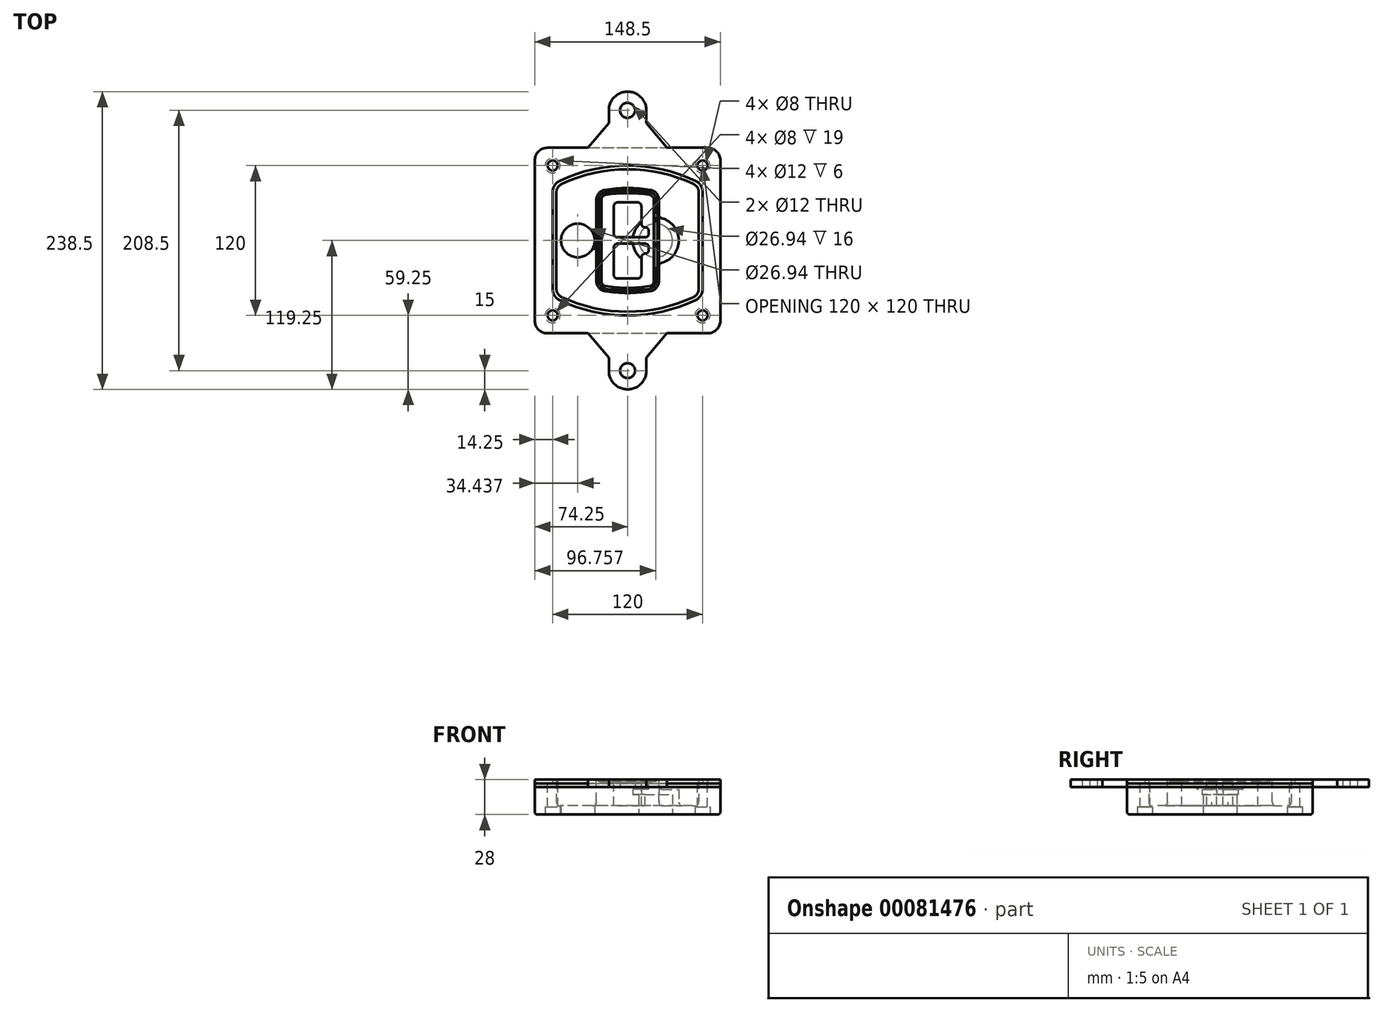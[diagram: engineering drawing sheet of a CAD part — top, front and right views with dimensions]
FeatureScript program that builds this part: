
annotation { "Feature Type Name" : "Feature", "Feature Type Description" : "" }
export const myFeature = defineFeature(function(context is Context, id is Id, definition is map)
    precondition{}
    {
        {
            var Q0;
            Q0=qCreatedBy(makeId("Top.planeOp"),FACE);
            var sketch = newSketch(context, id + "F0", { "sketchPlane" : qUnion([Q0])});
            skPoint(sketch, "E0.rect.middle", {"position": v(0, 0) * mm});
            skLineSegment(sketch, "E1.bottom", {"start": v(-64.25, -74.25) * mm, "end": v(64.25, -74.25) * mm});
            skLineSegment(sketch, "E1.top", {"start": v(-64.25, 74.25) * mm, "end": v(64.25, 74.25) * mm});
            skLineSegment(sketch, "E1.left", {"start": v(-74.25, -64.25) * mm, "end": v(-74.25, 64.25) * mm});
            skLineSegment(sketch, "E1.right", {"start": v(74.25, -64.25) * mm, "end": v(74.25, 64.25) * mm});
            skLineSegment(sketch, "E2", {"start": v(-74.25, 74.25) * mm, "end": v(74.25, -74.25) * mm, "construction": true});
            skLineSegment(sketch, "E3", {"start": v(74.25, 74.25) * mm, "end": v(-74.25, -74.25) * mm, "construction": true});
            skCircle(sketch, "E4", {"center": v(-60, 60) * mm, "radius": 4 * mm});
            skCircle(sketch, "E5", {"center": v(60, 60) * mm, "radius": 4 * mm});
            skCircle(sketch, "E6", {"center": v(60, -60) * mm, "radius": 4 * mm});
            skCircle(sketch, "E7", {"center": v(-60, -60) * mm, "radius": 4 * mm});
            skLineSegment(sketch, "E8", {"start": v(-60, 60) * mm, "end": v(60, 60) * mm, "construction": true});
            skLineSegment(sketch, "E9", {"start": v(60, 60) * mm, "end": v(60, -60) * mm, "construction": true});
            skLineSegment(sketch, "E10", {"start": v(60, -60) * mm, "end": v(-60, -60) * mm, "construction": true});
            skLineSegment(sketch, "E11", {"start": v(-60, -60) * mm, "end": v(-60, 60) * mm, "construction": true});
            skLineSegment(sketch, "E12", {"start": v(-60, 38.83) * mm, "end": v(-60, -38.83) * mm});
            skLineSegment(sketch, "E13", {"start": v(60, 38.83) * mm, "end": v(60, -38.83) * mm});
            skArc(sketch, "E14", {"start": v(54.26, 47.88) * mm, "mid": v(0, 60) * mm, "end": v(-54.26, 47.88) * mm});
            skArc(sketch, "E15", {"start": v(-54.26, -47.88) * mm, "mid": v(0, -60) * mm, "end": v(54.26, -47.88) * mm});
            skLineSegment(sketch, "E16", {"start": v(-60, 0) * mm, "end": v(60, 0) * mm, "construction": true});
            skPoint(sketch, "E17.visualSharp", {"position": v(-60, -45) * mm});
            skArc(sketch, "E17.filletArc", {"start": v(-60, -38.83) * mm, "mid": v(-58.44, -44.2) * mm, "end": v(-54.26, -47.88) * mm});
            skPoint(sketch, "E18.visualSharp", {"position": v(-60, 45) * mm});
            skArc(sketch, "E18.filletArc", {"start": v(-54.26, 47.88) * mm, "mid": v(-58.44, 44.2) * mm, "end": v(-60, 38.83) * mm});
            skPoint(sketch, "E19.visualSharp", {"position": v(60, 45) * mm});
            skArc(sketch, "E19.filletArc", {"start": v(60, 38.83) * mm, "mid": v(58.44, 44.2) * mm, "end": v(54.26, 47.88) * mm});
            skPoint(sketch, "E20.visualSharp", {"position": v(60, -45) * mm});
            skArc(sketch, "E20.filletArc", {"start": v(54.26, -47.88) * mm, "mid": v(58.44, -44.2) * mm, "end": v(60, -38.83) * mm});
            skPoint(sketch, "E21.visualSharp", {"position": v(-74.25, 74.25) * mm});
            skArc(sketch, "E21.filletArc", {"start": v(-64.25, 74.25) * mm, "mid": v(-71.32, 71.32) * mm, "end": v(-74.25, 64.25) * mm});
            skPoint(sketch, "E22.visualSharp", {"position": v(74.25, 74.25) * mm});
            skArc(sketch, "E22.filletArc", {"start": v(74.25, 64.25) * mm, "mid": v(71.32, 71.32) * mm, "end": v(64.25, 74.25) * mm});
            skPoint(sketch, "E23.visualSharp", {"position": v(74.25, -74.25) * mm});
            skArc(sketch, "E23.filletArc", {"start": v(64.25, -74.25) * mm, "mid": v(71.32, -71.32) * mm, "end": v(74.25, -64.25) * mm});
            skPoint(sketch, "E24.visualSharp", {"position": v(-74.25, -74.25) * mm});
            skArc(sketch, "E24.filletArc", {"start": v(-74.25, -64.25) * mm, "mid": v(-71.32, -71.32) * mm, "end": v(-64.25, -74.25) * mm});
            skArc(sketch, "E25.0", {"start": v(57, 38.83) * mm, "mid": v(55.9, 42.58) * mm, "end": v(52.98, 45.17) * mm});
            skLineSegment(sketch, "E25.1", {"start": v(57, 38.83) * mm, "end": v(57, -38.83) * mm});
            skArc(sketch, "E25.2", {"start": v(52.98, -45.17) * mm, "mid": v(55.9, -42.58) * mm, "end": v(57, -38.83) * mm});
            skArc(sketch, "E25.3", {"start": v(-52.98, -45.17) * mm, "mid": v(0, -57) * mm, "end": v(52.98, -45.17) * mm});
            skArc(sketch, "E25.4", {"start": v(-57, -38.83) * mm, "mid": v(-55.9, -42.58) * mm, "end": v(-52.98, -45.17) * mm});
            skArc(sketch, "E25.5", {"start": v(52.98, 45.17) * mm, "mid": v(0, 57) * mm, "end": v(-52.98, 45.17) * mm});
            skLineSegment(sketch, "E25.6", {"start": v(-57, 38.83) * mm, "end": v(-57, -38.83) * mm});
            skArc(sketch, "E25.7", {"start": v(-52.98, 45.17) * mm, "mid": v(-55.9, 42.58) * mm, "end": v(-57, 38.83) * mm});
            skArc(sketch, "E26.0", {"start": v(-55.96, 51.5) * mm, "mid": v(-61.82, 46.33) * mm, "end": v(-64, 38.83) * mm});
            skArc(sketch, "E26.1", {"start": v(55.96, 51.5) * mm, "mid": v(0, 64) * mm, "end": v(-55.96, 51.5) * mm});
            skArc(sketch, "E26.2", {"start": v(64, 38.83) * mm, "mid": v(61.82, 46.33) * mm, "end": v(55.96, 51.5) * mm});
            skLineSegment(sketch, "E26.3", {"start": v(64, 38.83) * mm, "end": v(64, -38.83) * mm});
            skArc(sketch, "E26.4", {"start": v(55.96, -51.5) * mm, "mid": v(61.82, -46.33) * mm, "end": v(64, -38.83) * mm});
            skLineSegment(sketch, "E26.5", {"start": v(-64, 38.83) * mm, "end": v(-64, -38.83) * mm});
            skArc(sketch, "E26.6", {"start": v(-55.96, -51.5) * mm, "mid": v(0, -64) * mm, "end": v(55.96, -51.5) * mm});
            skArc(sketch, "E26.7", {"start": v(-64, -38.83) * mm, "mid": v(-61.82, -46.33) * mm, "end": v(-55.96, -51.5) * mm});
            skSolve(sketch);
        }
        {
            var Q0;
            Q0=makeQuery(id+"F0.imprint","IMPRINT",FACE,{"disambiguationData":[TD([[makeQuery(id+"F0.imprint","IMPRINT",EDGE,{"derivedFrom":sQuery(id+"F0.wireOp",EDGE,"E1.bottom")}),1.0]])]});
            var Q1;
            Q1=makeQuery(id+"F0.imprint","IMPRINT",FACE,{"disambiguationData":[TD([[makeQuery(id+"F0.imprint","IMPRINT",EDGE,{"derivedFrom":sQuery(id+"F0.wireOp",EDGE,"E12")}),1.0]])]});
            var Q2;
            Q2=makeQuery(id+"F0.imprint","IMPRINT",FACE,{"disambiguationData":[TD([[makeQuery(id+"F0.imprint","IMPRINT",EDGE,{"derivedFrom":sQuery(id+"F0.wireOp",EDGE,"E25.0")}),1.0]])]});
            var Q3;
            Q3=makeQuery(id+"F0.imprint","IMPRINT",FACE,{"disambiguationData":[TD([[makeQuery(id+"F0.imprint","IMPRINT",EDGE,{"derivedFrom":sQuery(id+"F0.wireOp",EDGE,"E12")}),-1.0]])]});
            extrude(context, id + "F1", {"entities" : qUnion([Q0, Q1, Q2, Q3]), "oppositeDirection" : true, "depth" : 25 * mm});
        }
        {
            var Q0;
            Q0=makeQuery(id+"F0.imprint","IMPRINT",FACE,{"disambiguationData":[TD([[makeQuery(id+"F0.imprint","IMPRINT",EDGE,{"derivedFrom":sQuery(id+"F0.wireOp",EDGE,"E12")}),1.0]])]});
            extrude(context, id + "F2", {"entities" : qUnion([Q0]), "operationType" : NewBodyOperationType.ADD, "depth" : 3 * mm});
        }
        {
            var Q0;
            Q0=makeQuery(id+"F0.imprint","IMPRINT",FACE,{"disambiguationData":[TD([[makeQuery(id+"F0.imprint","IMPRINT",EDGE,{"derivedFrom":sQuery(id+"F0.wireOp",EDGE,"E25.0")}),1.0]])]});
            extrude(context, id + "F3", {"entities" : qUnion([Q0]), "operationType" : NewBodyOperationType.REMOVE, "oppositeDirection" : true, "depth" : 18 * mm});
        }
        {
            var Q0;
            Q0=makeQuery(id+"F2.opExtrude","CAP_FACE",FACE,{"disambiguationData":[OSD([sQuery(id+"F0.wireOp",EDGE,"E12"),sQuery(id+"F0.wireOp",EDGE,"E13"),sQuery(id+"F0.wireOp",EDGE,"E14"),sQuery(id+"F0.wireOp",EDGE,"E15"),sQuery(id+"F0.wireOp",EDGE,"E17.filletArc"),sQuery(id+"F0.wireOp",EDGE,"E18.filletArc"),sQuery(id+"F0.wireOp",EDGE,"E19.filletArc"),sQuery(id+"F0.wireOp",EDGE,"E20.filletArc"),sQuery(id+"F0.wireOp",EDGE,"E25.0"),sQuery(id+"F0.wireOp",EDGE,"E25.1"),sQuery(id+"F0.wireOp",EDGE,"E25.2"),sQuery(id+"F0.wireOp",EDGE,"E25.3"),sQuery(id+"F0.wireOp",EDGE,"E25.4"),sQuery(id+"F0.wireOp",EDGE,"E25.5"),sQuery(id+"F0.wireOp",EDGE,"E25.6"),sQuery(id+"F0.wireOp",EDGE,"E25.7")])],"isStart":false});
            var sketch = newSketch(context, id + "F4", { "sketchPlane" : qUnion([Q0])});
            skArc(sketch, "E27.0", {"start": v(-18.34, -40.45) * mm, "mid": v(0, -42) * mm, "end": v(18.34, -40.45) * mm});
            skArc(sketch, "E28.0", {"start": v(18.34, 40.45) * mm, "mid": v(0, 42) * mm, "end": v(-18.34, 40.45) * mm});
            skLineSegment(sketch, "E29", {"start": v(-25, 32.57) * mm, "end": v(-25, -32.57) * mm});
            skLineSegment(sketch, "E30", {"start": v(25, 32.57) * mm, "end": v(25, -32.57) * mm});
            skLineSegment(sketch, "E31", {"start": v(-25, 39.1) * mm, "end": v(25, 39.1) * mm, "construction": true});
            skLineSegment(sketch, "E32", {"start": v(-25, -39.1) * mm, "end": v(25, -39.1) * mm, "construction": true});
            skPoint(sketch, "E33.visualSharp", {"position": v(-25, 39.1) * mm});
            skArc(sketch, "E33.filletArc", {"start": v(-18.34, 40.45) * mm, "mid": v(-23.11, 37.73) * mm, "end": v(-25, 32.57) * mm});
            skPoint(sketch, "E34.visualSharp", {"position": v(25, 39.1) * mm});
            skArc(sketch, "E34.filletArc", {"start": v(25, 32.57) * mm, "mid": v(23.11, 37.73) * mm, "end": v(18.34, 40.45) * mm});
            skPoint(sketch, "E35.visualSharp", {"position": v(25, -39.1) * mm});
            skArc(sketch, "E35.filletArc", {"start": v(18.34, -40.45) * mm, "mid": v(23.11, -37.73) * mm, "end": v(25, -32.57) * mm});
            skPoint(sketch, "E36.visualSharp", {"position": v(-25, -39.1) * mm});
            skArc(sketch, "E36.filletArc", {"start": v(-25, -32.57) * mm, "mid": v(-23.11, -37.73) * mm, "end": v(-18.34, -40.45) * mm});
            skArc(sketch, "E37.0", {"start": v(52.98, 45.17) * mm, "mid": v(0, 57) * mm, "end": v(-52.98, 45.17) * mm});
            skArc(sketch, "E37.1", {"start": v(-52.98, 45.17) * mm, "mid": v(-55.9, 42.58) * mm, "end": v(-57, 38.83) * mm});
            skLineSegment(sketch, "E37.2", {"start": v(-57, 38.83) * mm, "end": v(-57, -38.83) * mm});
            skArc(sketch, "E37.3", {"start": v(-57, -38.83) * mm, "mid": v(-55.9, -42.58) * mm, "end": v(-52.98, -45.17) * mm});
            skArc(sketch, "E37.4", {"start": v(-52.98, -45.17) * mm, "mid": v(0, -57) * mm, "end": v(52.98, -45.17) * mm});
            skArc(sketch, "E37.5", {"start": v(52.98, -45.17) * mm, "mid": v(55.9, -42.58) * mm, "end": v(57, -38.83) * mm});
            skLineSegment(sketch, "E37.6", {"start": v(57, 38.83) * mm, "end": v(57, -38.83) * mm});
            skArc(sketch, "E37.7", {"start": v(57, 38.83) * mm, "mid": v(55.9, 42.58) * mm, "end": v(52.98, 45.17) * mm});
            skLineSegment(sketch, "E38.0", {"start": v(23, 32.57) * mm, "end": v(23, -32.57) * mm});
            skArc(sketch, "E38.1", {"start": v(18, -38.48) * mm, "mid": v(21.58, -36.44) * mm, "end": v(23, -32.57) * mm});
            skArc(sketch, "E38.2", {"start": v(-18, -38.48) * mm, "mid": v(0, -40) * mm, "end": v(18, -38.48) * mm});
            skArc(sketch, "E38.3", {"start": v(-23, -32.57) * mm, "mid": v(-21.58, -36.44) * mm, "end": v(-18, -38.48) * mm});
            skLineSegment(sketch, "E38.4", {"start": v(-23, 32.57) * mm, "end": v(-23, -32.57) * mm});
            skArc(sketch, "E38.5", {"start": v(23, 32.57) * mm, "mid": v(21.58, 36.44) * mm, "end": v(18, 38.48) * mm});
            skArc(sketch, "E38.6", {"start": v(-18, 38.48) * mm, "mid": v(-21.58, 36.44) * mm, "end": v(-23, 32.57) * mm});
            skArc(sketch, "E38.7", {"start": v(18, 38.48) * mm, "mid": v(0, 40) * mm, "end": v(-18, 38.48) * mm});
            skArc(sketch, "E39.0", {"start": v(21, 32.57) * mm, "mid": v(20.06, 35.15) * mm, "end": v(17.67, 36.5) * mm});
            skLineSegment(sketch, "E39.1", {"start": v(21, 32.57) * mm, "end": v(21, -32.57) * mm});
            skArc(sketch, "E39.2", {"start": v(17.67, -36.5) * mm, "mid": v(20.06, -35.15) * mm, "end": v(21, -32.57) * mm});
            skArc(sketch, "E39.3", {"start": v(-17.67, -36.5) * mm, "mid": v(0, -38) * mm, "end": v(17.67, -36.5) * mm});
            skArc(sketch, "E39.4", {"start": v(-21, -32.57) * mm, "mid": v(-20.06, -35.15) * mm, "end": v(-17.67, -36.5) * mm});
            skArc(sketch, "E39.5", {"start": v(17.67, 36.5) * mm, "mid": v(0, 38) * mm, "end": v(-17.67, 36.5) * mm});
            skLineSegment(sketch, "E39.6", {"start": v(-21, 32.57) * mm, "end": v(-21, -32.57) * mm});
            skArc(sketch, "E39.7", {"start": v(-17.67, 36.5) * mm, "mid": v(-20.06, 35.15) * mm, "end": v(-21, 32.57) * mm});
            skLineSegment(sketch, "E40", {"start": v(-25, 0) * mm, "end": v(25, 0) * mm, "construction": true});
            skLineSegment(sketch, "E41", {"start": v(-11, 5.5) * mm, "end": v(-11, 27.5) * mm});
            skLineSegment(sketch, "E42", {"start": v(-8, 30.5) * mm, "end": v(8, 30.5) * mm});
            skLineSegment(sketch, "E43", {"start": v(11, 27.5) * mm, "end": v(11, 13.5) * mm});
            skLineSegment(sketch, "E44", {"start": v(14, 10.5) * mm, "end": v(14, 10.5) * mm});
            skLineSegment(sketch, "E45", {"start": v(17, 7.5) * mm, "end": v(17, 5.5) * mm});
            skLineSegment(sketch, "E46", {"start": v(14, 2.5) * mm, "end": v(-8, 2.5) * mm});
            skPoint(sketch, "E47.visualSharp", {"position": v(-11, 30.5) * mm});
            skArc(sketch, "E47.filletArc", {"start": v(-8, 30.5) * mm, "mid": v(-10.12, 29.62) * mm, "end": v(-11, 27.5) * mm});
            skPoint(sketch, "E48.visualSharp", {"position": v(11, 30.5) * mm});
            skArc(sketch, "E48.filletArc", {"start": v(11, 27.5) * mm, "mid": v(10.12, 29.62) * mm, "end": v(8, 30.5) * mm});
            skPoint(sketch, "E49.visualSharp", {"position": v(11, 10.5) * mm});
            skArc(sketch, "E49.filletArc", {"start": v(11, 13.5) * mm, "mid": v(11.88, 11.38) * mm, "end": v(14, 10.5) * mm});
            skPoint(sketch, "E50.visualSharp", {"position": v(17, 10.5) * mm});
            skArc(sketch, "E50.filletArc", {"start": v(17, 7.5) * mm, "mid": v(16.12, 9.62) * mm, "end": v(14, 10.5) * mm});
            skPoint(sketch, "E51.visualSharp", {"position": v(17, 2.5) * mm});
            skArc(sketch, "E51.filletArc", {"start": v(14, 2.5) * mm, "mid": v(16.12, 3.38) * mm, "end": v(17, 5.5) * mm});
            skPoint(sketch, "E52.visualSharp", {"position": v(-11, 2.5) * mm});
            skArc(sketch, "E52.filletArc", {"start": v(-11, 5.5) * mm, "mid": v(-10.12, 3.38) * mm, "end": v(-8, 2.5) * mm});
            skLineSegment(sketch, "E53.0.MirrorCS", {"start": v(14, -2.5) * mm, "end": v(-8, -2.5) * mm});
            skArc(sketch, "E54.0.MirrorCS", {"start": v(-11, -5.5) * mm, "mid": v(-10.12, -3.38) * mm, "end": v(-8, -2.5) * mm});
            skLineSegment(sketch, "E55.0.MirrorCS", {"start": v(-11, -5.5) * mm, "end": v(-11, -27.5) * mm});
            skArc(sketch, "E56.0.MirrorCS", {"start": v(-8, -30.5) * mm, "mid": v(-10.12, -29.62) * mm, "end": v(-11, -27.5) * mm});
            skLineSegment(sketch, "E57.0.MirrorCS", {"start": v(-8, -30.5) * mm, "end": v(8, -30.5) * mm});
            skArc(sketch, "E58.0.MirrorCS", {"start": v(11, -27.5) * mm, "mid": v(10.12, -29.62) * mm, "end": v(8, -30.5) * mm});
            skLineSegment(sketch, "E59.0.MirrorCS", {"start": v(11, -27.5) * mm, "end": v(11, -13.5) * mm});
            skArc(sketch, "E60.0.MirrorCS", {"start": v(11, -13.5) * mm, "mid": v(11.88, -11.38) * mm, "end": v(14, -10.5) * mm});
            skArc(sketch, "E61.0.MirrorCS", {"start": v(17, -7.5) * mm, "mid": v(16.12, -9.62) * mm, "end": v(14, -10.5) * mm});
            skLineSegment(sketch, "E62.0.MirrorCS", {"start": v(17, -7.5) * mm, "end": v(17, -5.5) * mm});
            skArc(sketch, "E63.0.MirrorCS", {"start": v(14, -2.5) * mm, "mid": v(16.12, -3.38) * mm, "end": v(17, -5.5) * mm});
            skSolve(sketch);
        }
        {
            var Q0;
            Q0=makeQuery(id+"F4.imprint","IMPRINT",FACE,{"disambiguationData":[TD([[makeQuery(id+"F4.imprint","IMPRINT",EDGE,{"derivedFrom":sQuery(id+"F4.wireOp",EDGE,"E27.0")}),1.0]])]});
            var Q1;
            Q1=makeQuery(id+"F4.imprint","IMPRINT",FACE,{"disambiguationData":[TD([[makeQuery(id+"F4.imprint","IMPRINT",EDGE,{"derivedFrom":sQuery(id+"F4.wireOp",EDGE,"E38.0")}),-1.0]])]});
            var Q2;
            Q2=makeQuery(id+"F4.imprint","IMPRINT",FACE,{"disambiguationData":[TD([[makeQuery(id+"F4.imprint","IMPRINT",EDGE,{"derivedFrom":sQuery(id+"F4.wireOp",EDGE,"E39.0")}),1.0]])]});
            extrude(context, id + "F5", {"entities" : qUnion([Q0, Q1, Q2]), "operationType" : NewBodyOperationType.ADD, "endBound" : BoundingType.UP_TO_NEXT, "oppositeDirection" : true, "depth" : 25 * mm});
        }
        {
            var Q0;
            Q0=makeQuery(id+"F4.imprint","IMPRINT",FACE,{"disambiguationData":[TD([[makeQuery(id+"F4.imprint","IMPRINT",EDGE,{"derivedFrom":sQuery(id+"F4.wireOp",EDGE,"E38.0")}),-1.0]])]});
            extrude(context, id + "F6", {"entities" : qUnion([Q0]), "operationType" : NewBodyOperationType.REMOVE, "oppositeDirection" : true, "depth" : 2 * mm});
        }
        {
            var Q0;
            Q0=makeQuery(id+"F1.opExtrude","CAP_FACE",FACE,{"disambiguationData":[OSD([sQuery(id+"F0.wireOp",EDGE,"E1.bottom"),sQuery(id+"F0.wireOp",EDGE,"E1.top"),sQuery(id+"F0.wireOp",EDGE,"E1.left"),sQuery(id+"F0.wireOp",EDGE,"E1.right"),sQuery(id+"F0.wireOp",EDGE,"E4"),sQuery(id+"F0.wireOp",EDGE,"E5"),sQuery(id+"F0.wireOp",EDGE,"E6"),sQuery(id+"F0.wireOp",EDGE,"E7"),sQuery(id+"F0.wireOp",EDGE,"E21.filletArc"),sQuery(id+"F0.wireOp",EDGE,"E22.filletArc"),sQuery(id+"F0.wireOp",EDGE,"E23.filletArc"),sQuery(id+"F0.wireOp",EDGE,"E24.filletArc")])],"isStart":false});
            var sketch = newSketch(context, id + "F7", { "sketchPlane" : qUnion([Q0])});
            skCircle(sketch, "E64", {"center": v(22.5, 0) * mm, "radius": 13.47 * mm});
            skCircle(sketch, "E65", {"center": v(-39.81, 0) * mm, "radius": 13.47 * mm});
            skLineSegment(sketch, "E66", {"start": v(74.25, 0) * mm, "end": v(-74.25, 0) * mm});
            skCircle(sketch, "E67", {"center": v(22.5, 0) * mm, "radius": 18.47 * mm});
            skCircle(sketch, "E68", {"center": v(60, -60) * mm, "radius": 6 * mm});
            skCircle(sketch, "E69", {"center": v(-60, -60) * mm, "radius": 6 * mm});
            skCircle(sketch, "E70", {"center": v(-60, 60) * mm, "radius": 6 * mm});
            skCircle(sketch, "E71", {"center": v(60, 60) * mm, "radius": 6 * mm});
            skSolve(sketch);
        }
        {
            var Q0;
            {var subQ1=sQuery(id+"F7.wireOp",EDGE,"E66");var subQ4=sQuery(id+"F7.wireOp",EDGE,"E64");var subQ6=makeQuery(id+"F7.imprint","INTERSECT",VERTEX,{"disambiguationData":[OD(0.0)],"derivedFrom":[subQ4,subQ1]});Q0=makeQuery(id+"F7.imprint","IMPRINT",FACE,{"disambiguationData":[TD([[makeQuery(id+"F7.imprint","IMPRINT",EDGE,{"disambiguationData":[TD([[subQ6,-1.0]])],"derivedFrom":subQ4}),-1.0]])]});}
            var Q1;
            {var subQ0=sQuery(id+"F7.wireOp",EDGE,"E66");var subQ1=sQuery(id+"F7.wireOp",EDGE,"E64");var subQ3=makeQuery(id+"F7.imprint","INTERSECT",VERTEX,{"disambiguationData":[OD(0.0)],"derivedFrom":[subQ1,subQ0]});Q1=makeQuery(id+"F7.imprint","IMPRINT",FACE,{"disambiguationData":[TD([[makeQuery(id+"F7.imprint","IMPRINT",EDGE,{"disambiguationData":[TD([[subQ3,-1.0]])],"derivedFrom":subQ1}),1.0]])]});}
            var Q2;
            {var subQ0=sQuery(id+"F7.wireOp",EDGE,"E66");var subQ1=sQuery(id+"F7.wireOp",EDGE,"E64");var subQ3=makeQuery(id+"F7.imprint","INTERSECT",VERTEX,{"disambiguationData":[OD(0.0)],"derivedFrom":[subQ1,subQ0]});Q2=makeQuery(id+"F7.imprint","IMPRINT",FACE,{"disambiguationData":[TD([[makeQuery(id+"F7.imprint","IMPRINT",EDGE,{"disambiguationData":[TD([[subQ3,1.0]])],"derivedFrom":subQ1}),1.0]])]});}
            var Q3;
            {var subQ1=sQuery(id+"F7.wireOp",EDGE,"E66");var subQ4=sQuery(id+"F7.wireOp",EDGE,"E64");var subQ6=makeQuery(id+"F7.imprint","INTERSECT",VERTEX,{"disambiguationData":[OD(0.0)],"derivedFrom":[subQ4,subQ1]});Q3=makeQuery(id+"F7.imprint","IMPRINT",FACE,{"disambiguationData":[TD([[makeQuery(id+"F7.imprint","IMPRINT",EDGE,{"disambiguationData":[TD([[subQ6,1.0]])],"derivedFrom":subQ4}),-1.0]])]});}
            extrude(context, id + "F8", {"entities" : qUnion([Q0, Q1, Q2, Q3]), "operationType" : NewBodyOperationType.ADD, "oppositeDirection" : true, "depth" : 20 * mm});
        }
        {
            var Q0;
            {var subQ0=sQuery(id+"F7.wireOp",EDGE,"E66");var subQ1=sQuery(id+"F7.wireOp",EDGE,"E64");var subQ3=makeQuery(id+"F7.imprint","INTERSECT",VERTEX,{"disambiguationData":[OD(0.0)],"derivedFrom":[subQ1,subQ0]});Q0=makeQuery(id+"F7.imprint","IMPRINT",FACE,{"disambiguationData":[TD([[makeQuery(id+"F7.imprint","IMPRINT",EDGE,{"disambiguationData":[TD([[subQ3,-1.0]])],"derivedFrom":subQ1}),1.0]])]});}
            var Q1;
            {var subQ0=sQuery(id+"F7.wireOp",EDGE,"E66");var subQ1=sQuery(id+"F7.wireOp",EDGE,"E64");var subQ3=makeQuery(id+"F7.imprint","INTERSECT",VERTEX,{"disambiguationData":[OD(0.0)],"derivedFrom":[subQ1,subQ0]});Q1=makeQuery(id+"F7.imprint","IMPRINT",FACE,{"disambiguationData":[TD([[makeQuery(id+"F7.imprint","IMPRINT",EDGE,{"disambiguationData":[TD([[subQ3,1.0]])],"derivedFrom":subQ1}),1.0]])]});}
            extrude(context, id + "F9", {"entities" : qUnion([Q0, Q1]), "operationType" : NewBodyOperationType.REMOVE, "oppositeDirection" : true, "depth" : 16 * mm});
        }
        {
            var Q0;
            {var subQ0=sQuery(id+"F7.wireOp",EDGE,"E66");var subQ1=sQuery(id+"F7.wireOp",EDGE,"E65");var subQ3=makeQuery(id+"F7.imprint","INTERSECT",VERTEX,{"disambiguationData":[OD(0.0)],"derivedFrom":[subQ1,subQ0]});Q0=makeQuery(id+"F7.imprint","IMPRINT",FACE,{"disambiguationData":[TD([[makeQuery(id+"F7.imprint","IMPRINT",EDGE,{"disambiguationData":[TD([[subQ3,-1.0]])],"derivedFrom":subQ1}),1.0]])]});}
            var Q1;
            {var subQ0=sQuery(id+"F7.wireOp",EDGE,"E66");var subQ1=sQuery(id+"F7.wireOp",EDGE,"E65");var subQ3=makeQuery(id+"F7.imprint","INTERSECT",VERTEX,{"disambiguationData":[OD(0.0)],"derivedFrom":[subQ1,subQ0]});Q1=makeQuery(id+"F7.imprint","IMPRINT",FACE,{"disambiguationData":[TD([[makeQuery(id+"F7.imprint","IMPRINT",EDGE,{"disambiguationData":[TD([[subQ3,1.0]])],"derivedFrom":subQ1}),1.0]])]});}
            extrude(context, id + "F10", {"entities" : qUnion([Q0, Q1]), "operationType" : NewBodyOperationType.REMOVE, "oppositeDirection" : true, "depth" : 25 * mm});
        }
        {
            var Q0;
            Q0=makeQuery(id+"F7.imprint","IMPRINT",FACE,{"disambiguationData":[TD([[makeQuery(id+"F7.imprint","IMPRINT",EDGE,{"derivedFrom":sQuery(id+"F7.wireOp",EDGE,"E68")}),1.0]])]});
            var Q1;
            Q1=makeQuery(id+"F7.imprint","IMPRINT",FACE,{"disambiguationData":[TD([[makeQuery(id+"F7.imprint","IMPRINT",EDGE,{"derivedFrom":makeQuery(id+"F1.opExtrude","CAP_EDGE",EDGE,{"disambiguationData":[OSD([sQuery(id+"F0.wireOp",EDGE,"E5")])],"isStart":false})}),-1.0]])]});
            var Q2;
            Q2=makeQuery(id+"F7.imprint","IMPRINT",FACE,{"disambiguationData":[TD([[makeQuery(id+"F7.imprint","IMPRINT",EDGE,{"derivedFrom":sQuery(id+"F7.wireOp",EDGE,"E69")}),1.0]])]});
            var Q3;
            Q3=makeQuery(id+"F7.imprint","IMPRINT",FACE,{"disambiguationData":[TD([[makeQuery(id+"F7.imprint","IMPRINT",EDGE,{"derivedFrom":makeQuery(id+"F1.opExtrude","CAP_EDGE",EDGE,{"disambiguationData":[OSD([sQuery(id+"F0.wireOp",EDGE,"E4")])],"isStart":false})}),-1.0]])]});
            var Q4;
            Q4=makeQuery(id+"F7.imprint","IMPRINT",FACE,{"disambiguationData":[TD([[makeQuery(id+"F7.imprint","IMPRINT",EDGE,{"derivedFrom":sQuery(id+"F7.wireOp",EDGE,"E70")}),1.0]])]});
            var Q5;
            Q5=makeQuery(id+"F7.imprint","IMPRINT",FACE,{"disambiguationData":[TD([[makeQuery(id+"F7.imprint","IMPRINT",EDGE,{"derivedFrom":makeQuery(id+"F1.opExtrude","CAP_EDGE",EDGE,{"disambiguationData":[OSD([sQuery(id+"F0.wireOp",EDGE,"E7")])],"isStart":false})}),-1.0]])]});
            var Q6;
            Q6=makeQuery(id+"F7.imprint","IMPRINT",FACE,{"disambiguationData":[TD([[makeQuery(id+"F7.imprint","IMPRINT",EDGE,{"derivedFrom":sQuery(id+"F7.wireOp",EDGE,"E71")}),1.0]])]});
            var Q7;
            Q7=makeQuery(id+"F7.imprint","IMPRINT",FACE,{"disambiguationData":[TD([[makeQuery(id+"F7.imprint","IMPRINT",EDGE,{"derivedFrom":makeQuery(id+"F1.opExtrude","CAP_EDGE",EDGE,{"disambiguationData":[OSD([sQuery(id+"F0.wireOp",EDGE,"E6")])],"isStart":false})}),-1.0]])]});
            extrude(context, id + "F11", {"entities" : qUnion([Q0, Q1, Q2, Q3, Q4, Q5, Q6, Q7]), "operationType" : NewBodyOperationType.REMOVE, "oppositeDirection" : true, "depth" : 6 * mm});
        }
        {
            var Q0;
            Q0=makeQuery(id+"F9.boolean.opBoolean","COPY",FACE,{"derivedFrom":makeQuery(id+"F9.opExtrude","CAP_FACE",FACE,{"disambiguationData":[OSD([sQuery(id+"F7.wireOp",EDGE,"E64")])],"isStart":false})});
            var sketch = newSketch(context, id + "F12", { "sketchPlane" : qUnion([Q0])});
            skArc(sketch, "E72.0", {"start": v(11, 14.45) * mm, "mid": v(6.45, 9.13) * mm, "end": v(4.2, 2.5) * mm});
            skArc(sketch, "E72.1", {"start": v(4.2, -2.5) * mm, "mid": v(6.45, -9.13) * mm, "end": v(11, -14.45) * mm});
            skLineSegment(sketch, "E73", {"start": v(4.2, -2.5) * mm, "end": v(14, -2.5) * mm});
            skLineSegment(sketch, "E74.0", {"start": v(14, 2.5) * mm, "end": v(4.2, 2.5) * mm});
            skArc(sketch, "E74.1", {"start": v(14, 2.5) * mm, "mid": v(16.12, 3.38) * mm, "end": v(17, 5.5) * mm});
            skLineSegment(sketch, "E74.2", {"start": v(17, 7.5) * mm, "end": v(17, 5.5) * mm});
            skArc(sketch, "E74.3", {"start": v(17, 7.5) * mm, "mid": v(16.12, 9.62) * mm, "end": v(14, 10.5) * mm});
            skArc(sketch, "E74.4", {"start": v(11, 13.5) * mm, "mid": v(11.88, 11.38) * mm, "end": v(14, 10.5) * mm});
            skLineSegment(sketch, "E74.5", {"start": v(11, 14.45) * mm, "end": v(11, 13.5) * mm});
            skLineSegment(sketch, "E74.7", {"start": v(14, -2.5) * mm, "end": v(4.2, -2.5) * mm});
            skArc(sketch, "E74.8", {"start": v(14, -2.5) * mm, "mid": v(16.12, -3.38) * mm, "end": v(17, -5.5) * mm});
            skLineSegment(sketch, "E74.9", {"start": v(17, -7.5) * mm, "end": v(17, -5.5) * mm});
            skArc(sketch, "E74.10", {"start": v(17, -7.5) * mm, "mid": v(16.12, -9.62) * mm, "end": v(14, -10.5) * mm});
            skArc(sketch, "E74.11", {"start": v(11, -13.5) * mm, "mid": v(11.88, -11.38) * mm, "end": v(14, -10.5) * mm});
            skLineSegment(sketch, "E74.12", {"start": v(11, -14.45) * mm, "end": v(11, -13.5) * mm});
            skPoint(sketch, "E75.orphan", {"position": v(11, -27.5) * mm});
            skPoint(sketch, "E76.orphan", {"position": v(-8, -2.5) * mm});
            skPoint(sketch, "E77.orphan", {"position": v(-8, 2.5) * mm});
            skPoint(sketch, "E78.orphan", {"position": v(11, 27.5) * mm});
            skSolve(sketch);
        }
        {
            var Q0;
            {var subQ7=sQuery(id+"F12.wireOp",EDGE,"E72.0");var subQ14=sQuery(id+"F12.wireOp",EDGE,"E72.1");var subQ16=sQuery(id+"F12.wireOp",EDGE,"E74.1");var subQ18=sQuery(id+"F12.wireOp",EDGE,"E74.8");Q0=qUnion([makeQuery(id+"F12.imprint","IMPRINT",FACE,{"disambiguationData":[TD([[makeQuery(id+"F12.imprint","IMPRINT",EDGE,{"derivedFrom":subQ7}),1.0]])]}),makeQuery(id+"F12.imprint","IMPRINT",FACE,{"disambiguationData":[TD([[makeQuery(id+"F12.imprint","IMPRINT",EDGE,{"derivedFrom":subQ14}),1.0]])]}),makeQuery(id+"F12.imprint","IMPRINT",FACE,{"disambiguationData":[TD([[makeQuery(id+"F12.imprint","IMPRINT",EDGE,{"derivedFrom":subQ16}),1.0]])]}),makeQuery(id+"F12.imprint","IMPRINT",FACE,{"disambiguationData":[TD([[makeQuery(id+"F12.imprint","IMPRINT",EDGE,{"derivedFrom":subQ18}),-1.0]])]})]);}
            var Q1;
            Q1=makeQuery(id+"F5.boolean.opBoolean","SPLIT",FACE,{"disambiguationData":[TD([makeQuery(id+"F5.opExtrude","SWEPT_FACE",FACE,{"disambiguationData":[OSD([sQuery(id+"F4.wireOp",EDGE,"E41")])]})])],"derivedFrom":makeQuery(id+"F3.boolean.opBoolean","COPY",FACE,{"derivedFrom":makeQuery(id+"F3.opExtrude","CAP_FACE",FACE,{"disambiguationData":[OSD([sQuery(id+"F0.wireOp",EDGE,"E25.0"),sQuery(id+"F0.wireOp",EDGE,"E25.1"),sQuery(id+"F0.wireOp",EDGE,"E25.2"),sQuery(id+"F0.wireOp",EDGE,"E25.3"),sQuery(id+"F0.wireOp",EDGE,"E25.4"),sQuery(id+"F0.wireOp",EDGE,"E25.5"),sQuery(id+"F0.wireOp",EDGE,"E25.6"),sQuery(id+"F0.wireOp",EDGE,"E25.7")])],"isStart":false})})});
            extrude(context, id + "F13", {"entities" : qUnion([Q0]), "operationType" : NewBodyOperationType.REMOVE, "endBound" : BoundingType.UP_TO_SURFACE, "endBoundEntityFace" : qUnion([Q1]), "depth" : 25 * mm});
        }
        {
            var Q0;
            Q0=makeQuery(id+"F3.boolean.opBoolean","COPY",EDGE,{"derivedFrom":makeQuery(id+"F3.opExtrude","CAP_EDGE",EDGE,{"disambiguationData":[OSD([sQuery(id+"F0.wireOp",EDGE,"E25.6")])],"isStart":false})});
            var Q1;
            Q1=makeQuery(id+"F8.boolean.opBoolean","INTERSECT",EDGE,{"derivedFrom":[makeQuery(id+"F5.opExtrude","SWEPT_FACE",FACE,{"disambiguationData":[OSD([sQuery(id+"F4.wireOp",EDGE,"E30")])]}),makeQuery(id+"F8.opExtrude","CAP_FACE",FACE,{"disambiguationData":[OSD([sQuery(id+"F7.wireOp",EDGE,"E67")])],"isStart":false})]});
            var Q2;
            Q2=makeQuery(id+"F8.boolean.opBoolean","INTERSECT",EDGE,{"disambiguationData":[OD(1.0)],"derivedFrom":[makeQuery(id+"F5.opExtrude","SWEPT_FACE",FACE,{"disambiguationData":[OSD([sQuery(id+"F4.wireOp",EDGE,"E30")])]}),makeQuery(id+"F8.opExtrude","SWEPT_FACE",FACE,{"disambiguationData":[OSD([sQuery(id+"F7.wireOp",EDGE,"E67")])]})]});
            var Q3;
            {var subQ0=sQuery(id+"F4.wireOp",EDGE,"E30");Q3=makeQuery(id+"F8.boolean.opBoolean","SPLIT",EDGE,{"disambiguationData":[TD([makeQuery(id+"F5.opExtrude","SWEPT_FACE",FACE,{"disambiguationData":[OSD([sQuery(id+"F4.wireOp",EDGE,"E35.filletArc")])]})])],"derivedFrom":makeQuery(id+"F5.opExtrude","CAP_EDGE",EDGE,{"disambiguationData":[OSD([subQ0])],"isStart":false})});}
            var Q4;
            {var subQ0=sQuery(id+"F0.wireOp",EDGE,"E25.7");var subQ1=sQuery(id+"F0.wireOp",EDGE,"E25.1");var subQ2=sQuery(id+"F0.wireOp",EDGE,"E25.6");var subQ3=sQuery(id+"F0.wireOp",EDGE,"E25.5");var subQ4=sQuery(id+"F0.wireOp",EDGE,"E25.4");var subQ5=sQuery(id+"F0.wireOp",EDGE,"E25.0");var subQ6=sQuery(id+"F0.wireOp",EDGE,"E25.2");var subQ7=sQuery(id+"F0.wireOp",EDGE,"E25.3");Q4=makeQuery(id+"F8.boolean.opBoolean","INTERSECT",EDGE,{"derivedFrom":[makeQuery(id+"F5.boolean.opBoolean","SPLIT",FACE,{"disambiguationData":[TD([makeQuery(id+"F2.opExtrude","SWEPT_FACE",FACE,{"disambiguationData":[OSD([subQ5])]})])],"derivedFrom":makeQuery(id+"F3.boolean.opBoolean","COPY",FACE,{"derivedFrom":makeQuery(id+"F3.opExtrude","CAP_FACE",FACE,{"disambiguationData":[OSD([subQ5,subQ1,subQ6,subQ7,subQ4,subQ3,subQ2,subQ0])],"isStart":false})})}),makeQuery(id+"F8.opExtrude","SWEPT_FACE",FACE,{"disambiguationData":[OSD([sQuery(id+"F7.wireOp",EDGE,"E67")])]})]});}
            var Q5;
            Q5=makeQuery(id+"F8.boolean.opBoolean","INTERSECT",EDGE,{"disambiguationData":[OD(0.0)],"derivedFrom":[makeQuery(id+"F5.opExtrude","SWEPT_FACE",FACE,{"disambiguationData":[OSD([sQuery(id+"F4.wireOp",EDGE,"E30")])]}),makeQuery(id+"F8.opExtrude","SWEPT_FACE",FACE,{"disambiguationData":[OSD([sQuery(id+"F7.wireOp",EDGE,"E67")])]})]});
            fillet(context, id + "F14", {"entities" : qUnion([Q0, Q1, Q2, Q3, Q4, Q5]), "radius" : 3 * mm, "tangentPropagation" : true, "allowEdgeOverflow" : false});
        }
        {
            var Q0;
            Q0=makeQuery(id+"F1.opExtrude","CAP_EDGE",EDGE,{"disambiguationData":[OSD([sQuery(id+"F0.wireOp",EDGE,"E1.bottom")])],"isStart":false});
            fillet(context, id + "F15", {"entities" : qUnion([Q0]), "radius" : 2 * mm, "tangentPropagation" : true, "allowEdgeOverflow" : false});
        }
        {
            var Q0;
            {var subQ0=sQuery(id+"F0.wireOp",EDGE,"E22.filletArc");var subQ1=sQuery(id+"F0.wireOp",EDGE,"E7");var subQ2=sQuery(id+"F0.wireOp",EDGE,"E6");var subQ3=sQuery(id+"F0.wireOp",EDGE,"E5");var subQ4=sQuery(id+"F0.wireOp",EDGE,"E4");var subQ5=sQuery(id+"F0.wireOp",EDGE,"E1.bottom");var subQ6=sQuery(id+"F0.wireOp",EDGE,"E21.filletArc");var subQ7=sQuery(id+"F0.wireOp",EDGE,"E1.top");var subQ8=sQuery(id+"F0.wireOp",EDGE,"E1.left");var subQ9=sQuery(id+"F0.wireOp",EDGE,"E1.right");var subQ10=sQuery(id+"F0.wireOp",EDGE,"E23.filletArc");var subQ11=sQuery(id+"F0.wireOp",EDGE,"E24.filletArc");Q0=makeQuery(id+"F2.boolean.opBoolean","SPLIT",FACE,{"disambiguationData":[TD([makeQuery(id+"F1.opExtrude","SWEPT_FACE",FACE,{"disambiguationData":[OSD([subQ5])]})])],"derivedFrom":makeQuery(id+"F1.opExtrude","CAP_FACE",FACE,{"disambiguationData":[OSD([subQ5,subQ7,subQ8,subQ9,subQ4,subQ3,subQ2,subQ1,subQ6,subQ0,subQ10,subQ11])],"isStart":true})});}
            var sketch = newSketch(context, id + "F16", { "sketchPlane" : qUnion([Q0])});
            skLineSegment(sketch, "E79", {"start": v(0, 104.25) * mm, "end": v(0, 74.25) * mm, "construction": true});
            skPoint(sketch, "E79.startSnap0", {"position": v(0, 74.25) * mm});
            skLineSegment(sketch, "E80", {"start": v(-31.67, 74.25) * mm, "end": v(-14.78, 94.03) * mm});
            skCircle(sketch, "E81", {"center": v(0, 104.25) * mm, "radius": 6 * mm});
            skLineSegment(sketch, "E82", {"start": v(31.54, 74.25) * mm, "end": v(15, 93.97) * mm});
            skLineSegment(sketch, "E83", {"start": v(-14.78, 94.03) * mm, "end": v(-15, 104.17) * mm});
            skLineSegment(sketch, "E84", {"start": v(15, 93.97) * mm, "end": v(15, 104.17) * mm});
            skArc(sketch, "E85", {"start": v(15, 104.17) * mm, "mid": v(0, 119.25) * mm, "end": v(-15, 104.17) * mm});
            skLineSegment(sketch, "E86", {"start": v(-74.25, 0) * mm, "end": v(74.25, 0) * mm, "construction": true});
            skLineSegment(sketch, "E87.MirrorCS", {"start": v(31.54, -74.25) * mm, "end": v(15, -93.97) * mm});
            skLineSegment(sketch, "E88.MirrorCS", {"start": v(-31.67, -74.25) * mm, "end": v(-14.78, -94.03) * mm});
            skLineSegment(sketch, "E89.MirrorCS", {"start": v(-14.78, -94.03) * mm, "end": v(-15, -104.17) * mm});
            skLineSegment(sketch, "E90.MirrorCS", {"start": v(15, -93.97) * mm, "end": v(15, -104.17) * mm});
            skArc(sketch, "E91.MirrorCS", {"start": v(15, -104.17) * mm, "mid": v(0, -119.25) * mm, "end": v(-15, -104.17) * mm});
            skCircle(sketch, "E92.MirrorC", {"center": v(0, -104.25) * mm, "radius": 6 * mm});
            skLineSegment(sketch, "E93.MirrorCS", {"start": v(0, -104.25) * mm, "end": v(0, -74.25) * mm, "construction": true});
            skSolve(sketch);
        }
        {
            var Q0;
            Q0=makeQuery(id+"F16.imprint","IMPRINT",FACE,{"disambiguationData":[TD([[makeQuery(id+"F16.imprint","IMPRINT",EDGE,{"derivedFrom":makeQuery(id+"F1.opExtrude","CAP_EDGE",EDGE,{"disambiguationData":[OSD([sQuery(id+"F0.wireOp",EDGE,"E1.left")])],"isStart":true})}),-1.0]])]});
            var Q1;
            {var subQ0=sQuery(id+"F16.wireOp",EDGE,"E87.MirrorCS");Q1=makeQuery(id+"F16.imprint","IMPRINT",FACE,{"disambiguationData":[TD([[makeQuery(id+"F16.imprint","IMPRINT",EDGE,{"derivedFrom":subQ0}),-1.0]])]});}
            var Q2;
            {var subQ1=sQuery(id+"F16.wireOp",EDGE,"E80");Q2=makeQuery(id+"F16.imprint","IMPRINT",FACE,{"disambiguationData":[TD([[makeQuery(id+"F16.imprint","IMPRINT",EDGE,{"derivedFrom":subQ1}),-1.0]])]});}
            extrude(context, id + "F17", {"entities" : qUnion([Q0, Q1, Q2]), "endBound" : BoundingType.SYMMETRIC, "depth" : 6 * mm});
        }
    });
